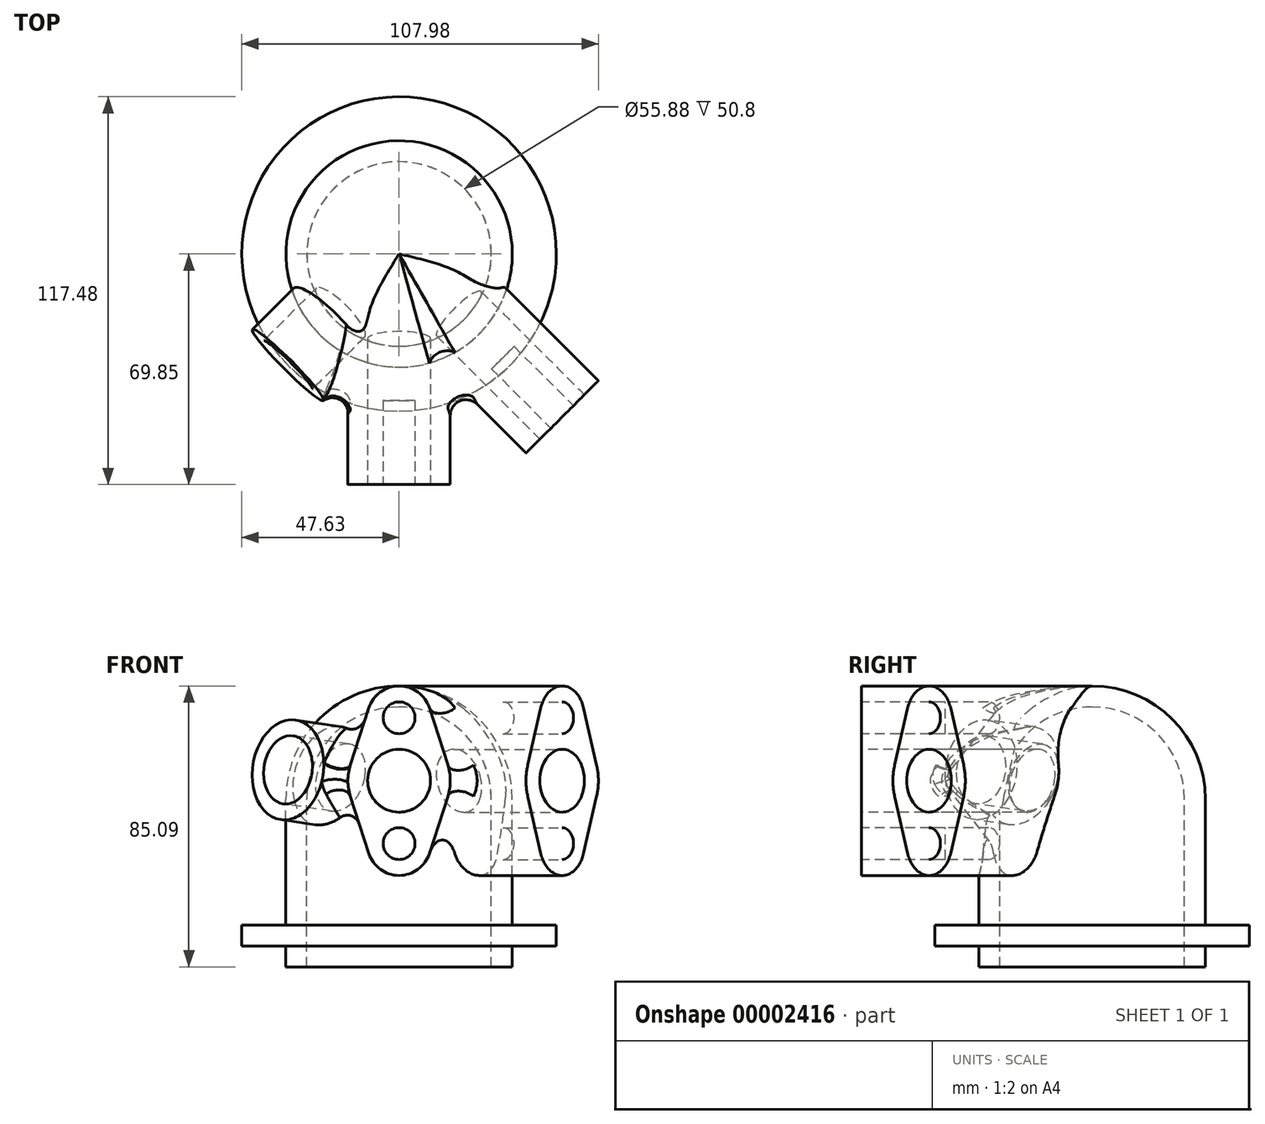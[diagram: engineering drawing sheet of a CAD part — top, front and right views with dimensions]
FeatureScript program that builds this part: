
annotation { "Feature Type Name" : "Feature", "Feature Type Description" : "" }
export const myFeature = defineFeature(function(context is Context, id is Id, definition is map)
    precondition{}
    {
        {
            var Q0;
            Q0=qCreatedBy(makeId("Top.planeOp"),FACE);
            var sketch = newSketch(context, id + "F0", { "sketchPlane" : qUnion([Q0])});
            skLineSegment(sketch, "E0", {"start": v(0, 0) * mm, "end": v(0, -64.05) * mm, "construction": true});
            skLineSegment(sketch, "E1", {"start": v(0, 0) * mm, "end": v(49.8, -49.8) * mm, "construction": true});
            skLineSegment(sketch, "E2.0.MirrorCS", {"start": v(0, 0) * mm, "end": v(-49.8, -49.8) * mm, "construction": true});
            skSolve(sketch);
        }
        {
            var Q0;
            Q0=qCreatedBy(makeId("Right.planeOp"),FACE);
            var sketch = newSketch(context, id + "F1", { "sketchPlane" : qUnion([Q0])});
            skLineSegment(sketch, "E3", {"start": v(0, 0) * mm, "end": v(0, 49.03) * mm, "construction": true});
            skSolve(sketch);
        }
        {
            var Q0;
            Q0=sQuery(id+"F1.wireOp",EDGE,"E3");
            cPlane(context, id + "F2", {"entities" : qUnion([Q0]), "cplaneType" : CPlaneType.LINE_ANGLE, "offset" : 152.4 * mm, "angle" : 135 * degree, "width" : 152.4 * mm, "height" : 152.4 * mm});
        }
        {
            var Q0;
            Q0=qCreatedBy(makeId("Front.planeOp"),FACE);
            var sketch = newSketch(context, id + "F3", { "sketchPlane" : qUnion([Q0])});
            skLineSegment(sketch, "E4", {"start": v(0, 0) * mm, "end": v(34.3, 0) * mm});
            skLineSegment(sketch, "E5", {"start": v(34.3, 0) * mm, "end": v(34.3, 6.35) * mm});
            skArc(sketch, "E6", {"start": v(34.3, 50.8) * mm, "mid": v(24.25, 75.05) * mm, "end": v(0, 85.1) * mm});
            skLineSegment(sketch, "E7.bottom", {"start": v(34.3, 12.7) * mm, "end": v(47.63, 12.7) * mm});
            skLineSegment(sketch, "E7.top", {"start": v(34.3, 6.35) * mm, "end": v(47.63, 6.35) * mm});
            skLineSegment(sketch, "E7.right", {"start": v(47.63, 12.7) * mm, "end": v(47.63, 6.35) * mm});
            skLineSegment(sketch, "E8.trimOffspring", {"start": v(34.3, 12.7) * mm, "end": v(34.3, 50.8) * mm});
            skLineSegment(sketch, "E9", {"start": v(0, 85.1) * mm, "end": v(0, 0) * mm});
            skSolve(sketch);
        }
        {
            var Q0;
            Q0=makeQuery(id+"F3.imprint","IMPRINT",FACE,{"disambiguationData":[TD([[makeQuery(id+"F3.imprint","IMPRINT",EDGE,{"derivedFrom":sQuery(id+"F3.wireOp",EDGE,"E4")}),1.0]])]});
            var Q1;
            Q1=sQuery(id+"F3.wireOp",EDGE,"E9");
            revolve(context, id + "F4", {"entities" : qUnion([Q0]), "axis" : qUnion([Q1]), "revolveType" : RevolveType.FULL});
        }
        {
            var Q0;
            Q0=makeQuery(id+"F4.opRevolve","SWEPT_FACE",FACE,{"disambiguationData":[OSD([sQuery(id+"F3.wireOp",EDGE,"E4")])]});
            shell(context, id + "F5", {"entities" : qUnion([Q0]), "thickness" : 6.35 * mm});
        }
        {
            var Q0;
            Q0=qCreatedBy(makeId("Front.planeOp"),FACE);
            cPlane(context, id + "F6", {"entities" : qUnion([Q0]), "cplaneType" : CPlaneType.OFFSET, "offset" : 69.85 * mm, "width" : 152.4 * mm, "height" : 152.4 * mm});
        }
        {
            var Q0;
            Q0=qCreatedBy(id+"F6.planeOp",FACE);
            var sketch = newSketch(context, id + "F7", { "sketchPlane" : qUnion([Q0])});
            skArc(sketch, "E10", {"start": v(-14.75, 61.14) * mm, "mid": v(-15.5, 56.39) * mm, "end": v(-14.75, 51.64) * mm});
            skLineSegment(sketch, "E11", {"start": v(0, 56.39) * mm, "end": v(37.25, 56.39) * mm, "construction": true});
            skArc(sketch, "E12", {"start": v(-9.19, 34.38) * mm, "mid": v(0, 27.69) * mm, "end": v(9.19, 34.38) * mm});
            skLineSegment(sketch, "E13", {"start": v(-14.75, 51.64) * mm, "end": v(-9.19, 34.38) * mm});
            skLineSegment(sketch, "E14", {"start": v(14.75, 51.64) * mm, "end": v(9.19, 34.38) * mm});
            skLineSegment(sketch, "E15.0.MirrorCS", {"start": v(-14.75, 61.14) * mm, "end": v(-9.19, 78.4) * mm});
            skLineSegment(sketch, "E15.1.MirrorCS", {"start": v(14.75, 61.14) * mm, "end": v(9.19, 78.4) * mm});
            skArc(sketch, "E15.2.MirrorC", {"start": v(-9.19, 78.4) * mm, "mid": v(0, 85.1) * mm, "end": v(9.19, 78.4) * mm});
            skArc(sketch, "E16.trimOffspring", {"start": v(14.75, 51.64) * mm, "mid": v(15.5, 56.39) * mm, "end": v(14.75, 61.14) * mm});
            skSolve(sketch);
        }
        {
            var Q0;
            Q0=makeQuery(id+"F7.imprint","IMPRINT",FACE,{"disambiguationData":[TD([[makeQuery(id+"F7.imprint","IMPRINT",EDGE,{"derivedFrom":sQuery(id+"F7.wireOp",EDGE,"E10")}),1.0]])]});
            extrude(context, id + "F8", {"entities" : qUnion([Q0]), "endBound" : BoundingType.UP_TO_NEXT, "oppositeDirection" : true, "depth" : 25.4 * mm});
        }
        {
            var Q0;
            Q0=makeQuery(id+"F8.opExtrude","CAP_FACE",FACE,{"disambiguationData":[OSD([sQuery(id+"F7.wireOp",EDGE,"E10"),sQuery(id+"F7.wireOp",EDGE,"E12"),sQuery(id+"F7.wireOp",EDGE,"E13"),sQuery(id+"F7.wireOp",EDGE,"E14"),sQuery(id+"F7.wireOp",EDGE,"E15.0.MirrorCS"),sQuery(id+"F7.wireOp",EDGE,"E15.1.MirrorCS"),sQuery(id+"F7.wireOp",EDGE,"E15.2.MirrorC"),sQuery(id+"F7.wireOp",EDGE,"E16.trimOffspring")])],"isStart":true});
            var sketch = newSketch(context, id + "F9", { "sketchPlane" : qUnion([Q0])});
            skCircle(sketch, "E17", {"center": v(0, 75.44) * mm, "radius": 4.83 * mm});
            skCircle(sketch, "E18", {"center": v(0, 37.34) * mm, "radius": 4.83 * mm});
            skSolve(sketch);
        }
        {
            var Q0;
            Q0=qSketchRegion(id+"F9",true);
            extrude(context, id + "F10", {"entities" : qUnion([Q0]), "operationType" : NewBodyOperationType.REMOVE, "oppositeDirection" : true, "depth" : 25.4 * mm});
        }
        {
            var Q0;
            Q0=makeQuery(id+"F8.opExtrude","SWEPT_BODY",BODY,{"disambiguationData":[OSD([sQuery(id+"F7.wireOp",EDGE,"E10"),sQuery(id+"F7.wireOp",EDGE,"E12"),sQuery(id+"F7.wireOp",EDGE,"E13"),sQuery(id+"F7.wireOp",EDGE,"E14"),sQuery(id+"F7.wireOp",EDGE,"E15.0.MirrorCS"),sQuery(id+"F7.wireOp",EDGE,"E15.1.MirrorCS"),sQuery(id+"F7.wireOp",EDGE,"E15.2.MirrorC"),sQuery(id+"F7.wireOp",EDGE,"E16.trimOffspring")])]});
            var Q1;
            Q1=sQuery(id+"F3.wireOp",EDGE,"E9");
            circularPattern(context, id + "F11", {"entities" : qUnion([Q0]), "axis" : qUnion([Q1]), "angle" : 45 * degree, "instanceCount" : 2, "oppositeDirection" : true});
        }
        {
            var Q0;
            Q0=qCreatedBy(id+"F2.planeOp",FACE);
            var sketch = newSketch(context, id + "F12", { "sketchPlane" : qUnion([Q0])});
            skLineSegment(sketch, "E19", {"start": v(0, 54.69) * mm, "end": v(47.58, 59.7) * mm, "construction": true});
            skLineSegment(sketch, "E20", {"start": v(0, 54.69) * mm, "end": v(47.58, 54.69) * mm, "construction": true});
            skSolve(sketch);
        }
        {
            var Q0;
            Q0=sQuery(id+"F12.wireOp",EDGE,"E19");
            var Q1;
            Q1=sQuery(id+"F12.wireOp",VERTEX,"E19.end");
            cPlane(context, id + "F13", {"entities" : qUnion([Q0, Q1]), "cplaneType" : CPlaneType.LINE_POINT, "offset" : 152.4 * mm, "width" : 152.4 * mm, "height" : 152.4 * mm});
        }
        {
            var Q0;
            Q0=qCreatedBy(id+"F13.planeOp",FACE);
            var sketch = newSketch(context, id + "F14", { "sketchPlane" : qUnion([Q0])});
            skCircle(sketch, "E21", {"center": v(5.65, 54.1) * mm, "radius": 15.24 * mm});
            skSolve(sketch);
        }
        {
            var Q0;
            Q0=makeQuery(id+"F14.imprint","IMPRINT",FACE,{"disambiguationData":[TD([[makeQuery(id+"F14.imprint","IMPRINT",EDGE,{"derivedFrom":sQuery(id+"F14.wireOp",EDGE,"E21")}),1.0]])]});
            var Q1;
            Q1=makeQuery(id+"F4.opRevolve","SWEPT_FACE",FACE,{"disambiguationData":[OSD([sQuery(id+"F3.wireOp",EDGE,"E8.trimOffspring")])]});
            extrude(context, id + "F15", {"entities" : qUnion([Q0]), "endBound" : BoundingType.UP_TO_BODY, "oppositeDirection" : true, "endBoundEntityBody" : qUnion([Q1]), "depth" : 25.4 * mm});
        }
        {
            var Q0;
            Q0=makeQuery(id+"F4.opRevolve","SWEPT_BODY",BODY,{"disambiguationData":[OSD([sQuery(id+"F3.wireOp",EDGE,"E4"),sQuery(id+"F3.wireOp",EDGE,"E5"),sQuery(id+"F3.wireOp",EDGE,"E6"),sQuery(id+"F3.wireOp",EDGE,"E7.bottom"),sQuery(id+"F3.wireOp",EDGE,"E7.top"),sQuery(id+"F3.wireOp",EDGE,"E7.right"),sQuery(id+"F3.wireOp",EDGE,"E8.trimOffspring"),sQuery(id+"F3.wireOp",EDGE,"E9")])]});
            var Q1;
            Q1=makeQuery(id+"F8.opExtrude","SWEPT_BODY",BODY,{"disambiguationData":[OSD([sQuery(id+"F7.wireOp",EDGE,"E10"),sQuery(id+"F7.wireOp",EDGE,"E12"),sQuery(id+"F7.wireOp",EDGE,"E13"),sQuery(id+"F7.wireOp",EDGE,"E14"),sQuery(id+"F7.wireOp",EDGE,"E15.0.MirrorCS"),sQuery(id+"F7.wireOp",EDGE,"E15.1.MirrorCS"),sQuery(id+"F7.wireOp",EDGE,"E15.2.MirrorC"),sQuery(id+"F7.wireOp",EDGE,"E16.trimOffspring")])]});
            var Q2;
            Q2=makeQuery(id+"F11.opPattern","COPY",BODY,{"derivedFrom":makeQuery(id+"F8.opExtrude","SWEPT_BODY",BODY,{"disambiguationData":[OSD([sQuery(id+"F7.wireOp",EDGE,"E10"),sQuery(id+"F7.wireOp",EDGE,"E12"),sQuery(id+"F7.wireOp",EDGE,"E13"),sQuery(id+"F7.wireOp",EDGE,"E14"),sQuery(id+"F7.wireOp",EDGE,"E15.0.MirrorCS"),sQuery(id+"F7.wireOp",EDGE,"E15.1.MirrorCS"),sQuery(id+"F7.wireOp",EDGE,"E15.2.MirrorC"),sQuery(id+"F7.wireOp",EDGE,"E16.trimOffspring")])]}),"instanceName":"1"});
            var Q3;
            Q3=makeQuery(id+"F15.opExtrude","SWEPT_BODY",BODY,{"disambiguationData":[OSD([sQuery(id+"F14.wireOp",EDGE,"E21")])]});
            booleanBodies(context, id + "F16", {"operationType" : BooleanOperationType.UNION, "tools" : qUnion([Q0, Q1, Q2, Q3])});
        }
        {
            var Q0;
            Q0=makeQuery(id+"F15.opExtrude","CAP_FACE",FACE,{"disambiguationData":[OSD([sQuery(id+"F14.wireOp",EDGE,"E21")])],"isStart":true});
            var sketch = newSketch(context, id + "F17", { "sketchPlane" : qUnion([Q0])});
            skCircle(sketch, "E22", {"center": v(5.65, 54.1) * mm, "radius": 10.41 * mm});
            skSolve(sketch);
        }
        {
            var Q0;
            Q0=qSketchRegion(id+"F17",true);
            extrude(context, id + "F18", {"entities" : qUnion([Q0]), "operationType" : NewBodyOperationType.REMOVE, "endBound" : BoundingType.UP_TO_NEXT, "oppositeDirection" : true, "depth" : 25.4 * mm});
        }
        {
            var Q0;
            Q0=makeQuery(id+"F8.opExtrude","CAP_FACE",FACE,{"disambiguationData":[OSD([sQuery(id+"F7.wireOp",EDGE,"E10"),sQuery(id+"F7.wireOp",EDGE,"E12"),sQuery(id+"F7.wireOp",EDGE,"E13"),sQuery(id+"F7.wireOp",EDGE,"E14"),sQuery(id+"F7.wireOp",EDGE,"E15.0.MirrorCS"),sQuery(id+"F7.wireOp",EDGE,"E15.1.MirrorCS"),sQuery(id+"F7.wireOp",EDGE,"E15.2.MirrorC"),sQuery(id+"F7.wireOp",EDGE,"E16.trimOffspring")])],"isStart":true});
            var sketch = newSketch(context, id + "F19", { "sketchPlane" : qUnion([Q0])});
            skCircle(sketch, "E23", {"center": v(0, 56.39) * mm, "radius": 9.53 * mm});
            skSolve(sketch);
        }
        {
            var Q0;
            Q0=qSketchRegion(id+"F19",true);
            extrude(context, id + "F20", {"entities" : qUnion([Q0]), "operationType" : NewBodyOperationType.REMOVE, "endBound" : BoundingType.UP_TO_NEXT, "oppositeDirection" : true, "depth" : 25.4 * mm});
        }
        {
            var Q0;
            Q0=makeQuery(id+"F11.opPattern","COPY",FACE,{"derivedFrom":makeQuery(id+"F8.opExtrude","CAP_FACE",FACE,{"disambiguationData":[OSD([sQuery(id+"F7.wireOp",EDGE,"E10"),sQuery(id+"F7.wireOp",EDGE,"E12"),sQuery(id+"F7.wireOp",EDGE,"E13"),sQuery(id+"F7.wireOp",EDGE,"E14"),sQuery(id+"F7.wireOp",EDGE,"E15.0.MirrorCS"),sQuery(id+"F7.wireOp",EDGE,"E15.1.MirrorCS"),sQuery(id+"F7.wireOp",EDGE,"E15.2.MirrorC"),sQuery(id+"F7.wireOp",EDGE,"E16.trimOffspring")])],"isStart":true}),"instanceName":"1"});
            var sketch = newSketch(context, id + "F21", { "sketchPlane" : qUnion([Q0])});
            skCircle(sketch, "E24", {"center": v(0, 56.39) * mm, "radius": 9.53 * mm});
            skSolve(sketch);
        }
        {
            var Q0;
            Q0=qSketchRegion(id+"F21",true);
            extrude(context, id + "F22", {"entities" : qUnion([Q0]), "operationType" : NewBodyOperationType.REMOVE, "endBound" : BoundingType.UP_TO_NEXT, "oppositeDirection" : true, "depth" : 25.4 * mm});
        }
        {
            var Q0;
            Q0=makeQuery(id+"F15.opExtrude","CAP_EDGE",EDGE,{"disambiguationData":[OSD([sQuery(id+"F14.wireOp",EDGE,"E21")]),topologyDisambiguationEdgeConnected([makeQuery(id+"F4.opRevolve","SWEPT_FACE",FACE,{"disambiguationData":[OSD([sQuery(id+"F3.wireOp",EDGE,"E6")])]})])],"isStart":false});
            var Q1;
            Q1=makeQuery(id+"F8.opExtrude","CAP_EDGE",EDGE,{"disambiguationData":[OSD([sQuery(id+"F7.wireOp",EDGE,"E15.2.MirrorC")]),OD(0.0)],"isStart":false});
            var Q2;
            Q2=makeQuery(id+"F8.opExtrude","CAP_EDGE",EDGE,{"disambiguationData":[OSD([sQuery(id+"F7.wireOp",EDGE,"E13")]),topologyDisambiguationEdgeConnected([makeQuery(id+"F4.opRevolve","SWEPT_FACE",FACE,{"disambiguationData":[OSD([sQuery(id+"F3.wireOp",EDGE,"E8.trimOffspring")])]})])],"isStart":false});
            var Q3;
            Q3=makeQuery(id+"F16.opBoolean","INTERSECT",EDGE,{"derivedFrom":[makeQuery(id+"F8.opExtrude","SWEPT_FACE",FACE,{"disambiguationData":[OSD([sQuery(id+"F7.wireOp",EDGE,"E15.0.MirrorCS")])]}),makeQuery(id+"F15.opExtrude","SWEPT_FACE",FACE,{"disambiguationData":[OSD([sQuery(id+"F14.wireOp",EDGE,"E21")])]})]});
            var Q4;
            Q4=makeQuery(id+"F11.opPattern","COPY",EDGE,{"derivedFrom":makeQuery(id+"F8.opExtrude","CAP_EDGE",EDGE,{"disambiguationData":[OSD([sQuery(id+"F7.wireOp",EDGE,"E12")])],"isStart":false}),"instanceName":"1"});
            var Q5;
            {var subQ0=makeQuery(id+"F8.opExtrude","SWEPT_FACE",FACE,{"disambiguationData":[OSD([sQuery(id+"F7.wireOp",EDGE,"E15.2.MirrorC")])]});Q5=makeQuery(id+"F16.opBoolean","INTERSECT",EDGE,{"derivedFrom":[subQ0,makeQuery(id+"F11.opPattern","COPY",FACE,{"derivedFrom":subQ0,"instanceName":"1"})]});}
            fillet(context, id + "F23", {"entities" : qUnion([Q0, Q1, Q2, Q3, Q4, Q5]), "radius" : 4.78 * mm, "tangentPropagation" : true, "allowEdgeOverflow" : false});
        }
    });
